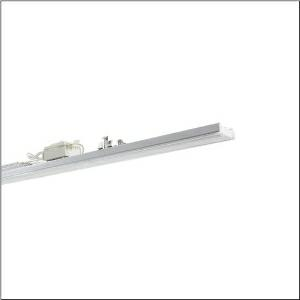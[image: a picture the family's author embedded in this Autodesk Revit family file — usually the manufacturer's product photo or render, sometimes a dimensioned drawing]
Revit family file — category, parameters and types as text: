
# Revit family: licross_21_recessed_mo_52tl12dn48xg
name_source: partatom
category: Lighting Fixtures
units: mm (PartAtom-declared; Revit-internal decimal feet)

## family parameters
Cut with Voids When Loaded = No
Host = Face
Light Source = No
Part Type = Normal
Room Calculation Point = No
Round Connector Dimension = Use Diameter
Shared = No

## types (1)
- --- (1 x LED, 8000 lm, 44.2 W, 4000K)
    Apparent Load = 44 VA
    CIE Flux Codes = 72 92 99 100 100
    Color Rendering = 80
    Color Temperature = 4000K
    Default Elevation = 1800 mm
    Description = Licross 21 Recessed MO, luminaire insert, of sheet steel, galvanised, coil coated, white, length: 1.500mm, width: 66mm, height: 67mm, LED rated luminous flux: 8.000lm, light colour: 840, SDCM (Standard Deviation of Colour Matching)MacAdam ≤ 3 SDCM (initial), control gear: DALI 2, with plug, 5-pole, with phase selection, mains connection: 220..240V, AC, 50/60Hz, rated input power: 44W, internal wiring halogen-free, primary optical cover: cover, of PMMA, light emission: direct distribution, primary light characteristic: symmetric, protection rating (complete): IP40, insulation class (complete): insulation class I (protective earthing), certification: CE, ENEC, VDE, UKCA, protection symbol: D if used in an environment without relevant dust loads with corresponding accessories, impact resistance: IK06, permissible ambient temperature for indoor applications: -25..+40°C, corresponds to IFS (International Featured Standards) requirements for safety and quality in the food industry, reducing of maximum allowable ambient temperature of 5°C with ceiling mounting, LABS conformity tested according to VDMA 24364:2018-05, The light source and the operating device comply with the requirements of the Ecodesign Regulation (EU) 2019/2020 and are replaceable in accordance with this regulation, packaging unit: 1 piece
    Height = 58 mm
    Lamp = 1 x LED
    Lamp Light Flux = 8000 lm
    Lamp Power = 44.2 W
    Lamp count = 1
    Length = 1500 mm
    Luminous efficacy = 181 lm/W
    Manufacturer = Siteco
    ModVariant = No
    Model = 52TL12DN48XG
    Mounting Place = Ceiling
    Mounting Type = Pendant
    Number of Poles = 1
    OnlyDefault = Yes
    Power Factor = 1
    Product Name = Licross 21 Recessed MO
    Product group = luminaire insert | ceiling pendant
    ProductGroupID = 901
    Protection Class = Protection class I
    Protection Degree = IP 40
    RLX_Detail_Level = 1
    RLX_Emergency_Light_Flux = 0 lm
    RLX_Emergency_Type = 0
    RLX_Emergency_Type_DB = No
    RlxData = <blob elided: 24853 chars, md5=a9a8e17c>
    Socket = socket
    Standby Power = 0 W
    System Light Flux = 8000 lm
    System Power = 44 W
    Type Comments = factory setting: luminous flux: 100 % | dim-lin: 254 | 297 mA
    Type Image = l_1296930.jpg
    URL = http://relux.com
    VarID = @adj_126341
    Voltage = 0 V
    Weight = 0.00 kg
    Width = 66 mm

## geometry (parser evidence)
native form markers: Blend x4, Sweep x13
no freeform markers — native parametric forms only
